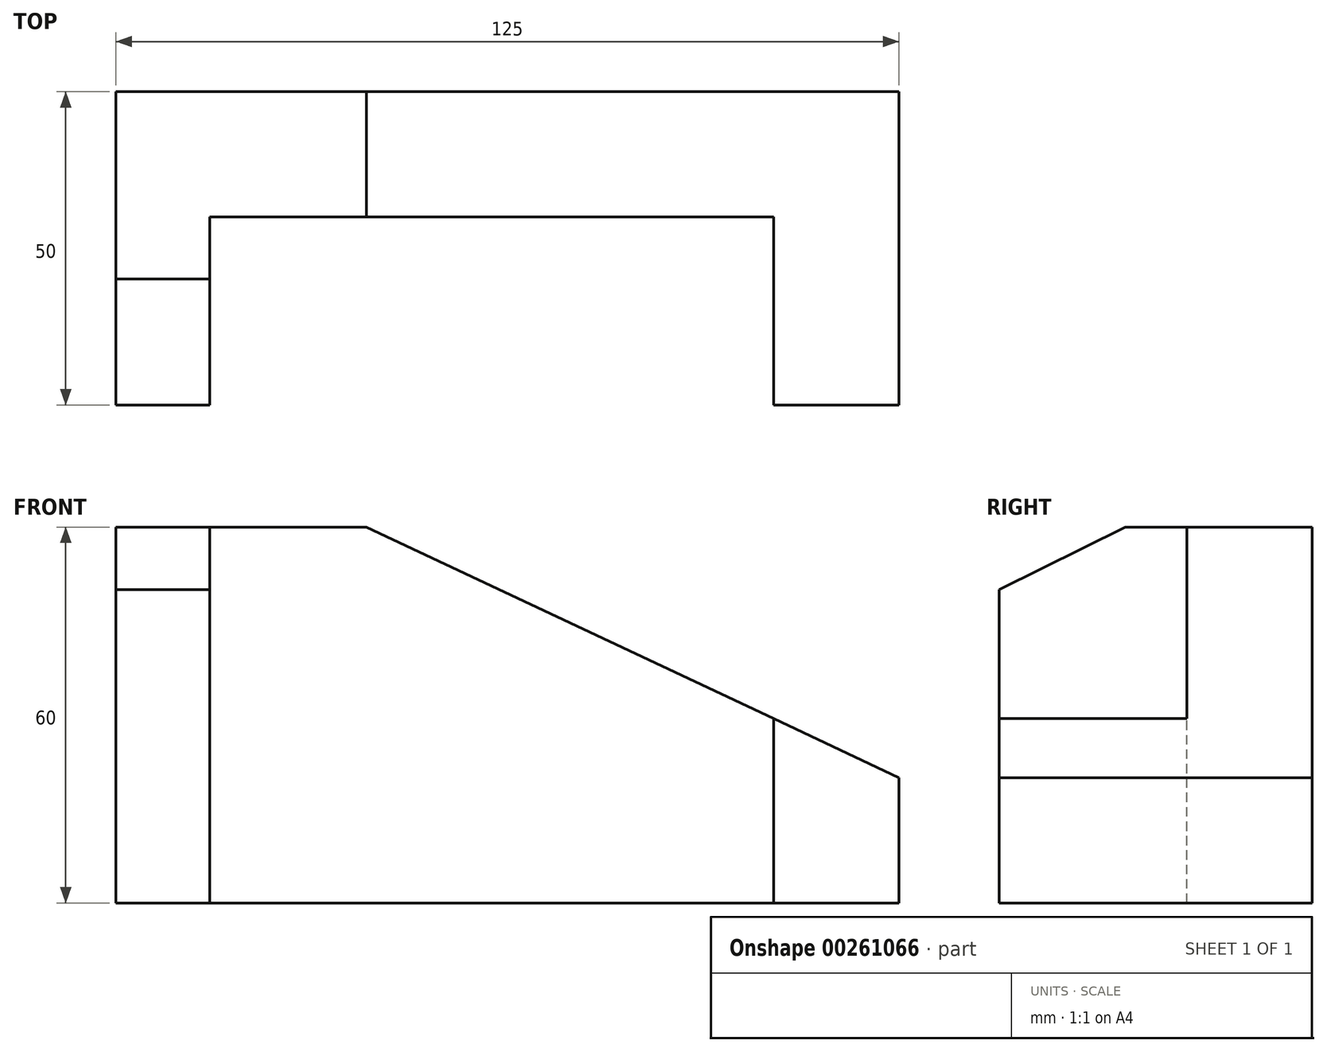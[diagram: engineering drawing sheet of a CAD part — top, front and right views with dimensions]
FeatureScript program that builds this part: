
annotation { "Feature Type Name" : "Feature", "Feature Type Description" : "" }
export const myFeature = defineFeature(function(context is Context, id is Id, definition is map)
    precondition{}
    {
        {
            assignVariable(context, id + "F0", {"name" : "C", "anyValue" : 50});
        }
        {
            var Q0;
            Q0=qCreatedBy(makeId("Front.planeOp"),FACE);
            var sketch = newSketch(context, id + "F1", { "sketchPlane" : qUnion([Q0])});
            skLineSegment(sketch, "E0", {"start": v(-65.44, 0) * mm, "end": v(-65.44, 60) * mm});
            skLineSegment(sketch, "E1", {"start": v(-65.44, 60) * mm, "end": v(-40.44, 60) * mm});
            skLineSegment(sketch, "E2", {"start": v(-40.44, 60) * mm, "end": v(44.56, 20) * mm});
            skLineSegment(sketch, "E3", {"start": v(44.56, 20) * mm, "end": v(44.56, 0) * mm});
            skLineSegment(sketch, "E4", {"start": v(44.56, 0) * mm, "end": v(-65.44, 0) * mm});
            skLineSegment(sketch, "E5", {"start": v(44.56, 0) * mm, "end": v(24.56, 0) * mm});
            skLineSegment(sketch, "E6", {"start": v(24.56, 0) * mm, "end": v(24.56, 29.41) * mm});
            skLineSegment(sketch, "E7", {"start": v(-65.44, 0) * mm, "end": v(-80.44, 0) * mm});
            skLineSegment(sketch, "E8", {"start": v(-80.44, 0) * mm, "end": v(-80.44, 60) * mm});
            skLineSegment(sketch, "E9", {"start": v(-80.44, 60) * mm, "end": v(-65.44, 60) * mm});
            skSolve(sketch);
        }
        {
            var Q0;
            Q0=makeQuery(id+"F1.imprint","IMPRINT",FACE,{"disambiguationData":[TD([[makeQuery(id+"F1.imprint","IMPRINT",EDGE,{"derivedFrom":sQuery(id+"F1.wireOp",EDGE,"E0")}),-1.0]])]});
            extrude(context, id + "F2", {"entities" : qUnion([Q0]), "oppositeDirection" : true, "depth" : (getVariable(context, 'C')) * mm});
        }
        {
            var Q0;
            Q0=makeQuery(id+"F2.opExtrude","CAP_FACE",FACE,{"disambiguationData":[OSD([sQuery(id+"F1.wireOp",EDGE,"E0"),sQuery(id+"F1.wireOp",EDGE,"E1"),sQuery(id+"F1.wireOp",EDGE,"E2"),sQuery(id+"F1.wireOp",EDGE,"E4"),sQuery(id+"F1.wireOp",EDGE,"E6")])],"isStart":true});
            extrude(context, id + "F3", {"entities" : qUnion([Q0]), "operationType" : NewBodyOperationType.REMOVE, "oppositeDirection" : true, "depth" : 30 * mm});
        }
        {
            var Q0;
            {var subQ0=sQuery(id+"F1.wireOp",EDGE,"E3");Q0=makeQuery(id+"F1.imprint","IMPRINT",FACE,{"disambiguationData":[TD([[makeQuery(id+"F1.imprint","IMPRINT",EDGE,{"derivedFrom":subQ0}),-1.0]])]});}
            extrude(context, id + "F4", {"entities" : qUnion([Q0]), "operationType" : NewBodyOperationType.ADD, "oppositeDirection" : true, "depth" : (getVariable(context, 'C')) * mm});
        }
        {
            var Q0;
            Q0=makeQuery(id+"F1.imprint","IMPRINT",FACE,{"disambiguationData":[TD([[makeQuery(id+"F1.imprint","IMPRINT",EDGE,{"derivedFrom":sQuery(id+"F1.wireOp",EDGE,"E0")}),1.0]])]});
            extrude(context, id + "F5", {"entities" : qUnion([Q0]), "operationType" : NewBodyOperationType.ADD, "oppositeDirection" : true, "depth" : (getVariable(context, 'C')) * mm});
        }
        {
            var Q0;
            Q0=makeQuery(id+"F5.opExtrude","SWEPT_FACE",FACE,{"disambiguationData":[OSD([sQuery(id+"F1.wireOp",EDGE,"E8")])]});
            var sketch = newSketch(context, id + "F6", { "sketchPlane" : qUnion([Q0])});
            skLineSegment(sketch, "E10", {"start": v(0, 50) * mm, "end": v(0, 60) * mm});
            skLineSegment(sketch, "E11", {"start": v(0, 60) * mm, "end": v(-20.12, 60) * mm});
            skLineSegment(sketch, "E12", {"start": v(-20.12, 60) * mm, "end": v(0, 50) * mm});
            skSolve(sketch);
        }
        {
            var Q0;
            Q0=makeQuery(id+"F6.imprint","IMPRINT",FACE,{"disambiguationData":[TD([[makeQuery(id+"F6.imprint","IMPRINT",EDGE,{"derivedFrom":sQuery(id+"F6.wireOp",EDGE,"E10")}),1.0]])]});
            extrude(context, id + "F7", {"entities" : qUnion([Q0]), "operationType" : NewBodyOperationType.REMOVE, "oppositeDirection" : true, "depth" : 15 * mm});
        }
    });
